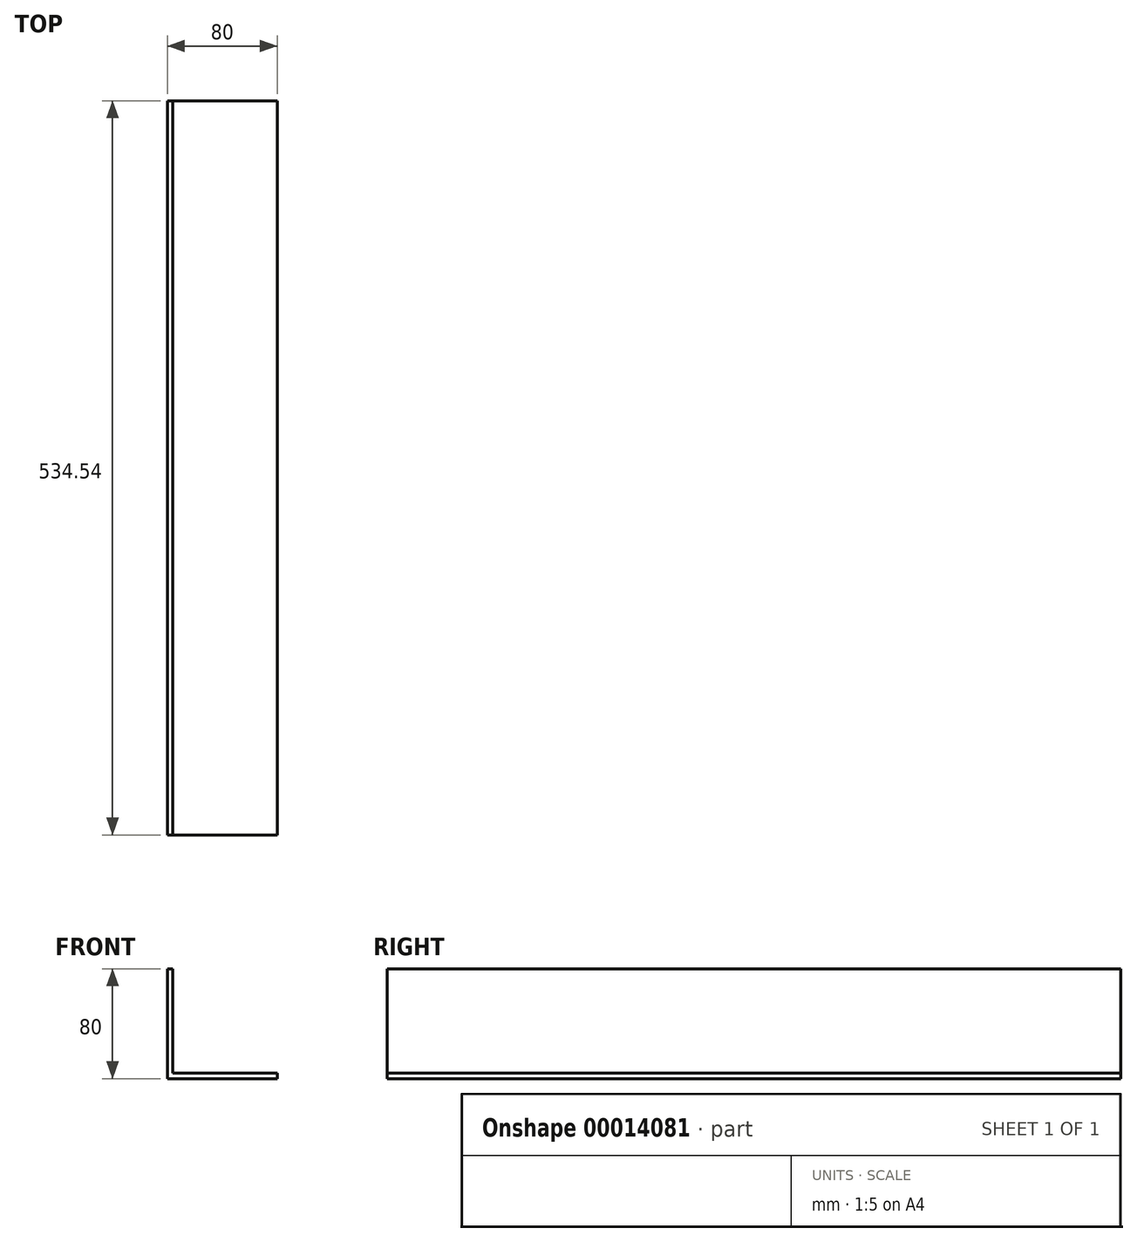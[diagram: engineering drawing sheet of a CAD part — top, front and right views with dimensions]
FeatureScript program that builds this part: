
annotation { "Feature Type Name" : "Feature", "Feature Type Description" : "" }
export const myFeature = defineFeature(function(context is Context, id is Id, definition is map)
    precondition{}
    {
        {
            var Q0;
            Q0=qCreatedBy(makeId("Front.planeOp"),FACE);
            var sketch = newSketch(context, id + "F0", { "sketchPlane" : qUnion([Q0])});
            skLineSegment(sketch, "E0.bottom", {"start": v(0, 0) * mm, "end": v(80, 0) * mm});
            skLineSegment(sketch, "E0.top", {"start": v(0, 80) * mm, "end": v(80, 80) * mm});
            skLineSegment(sketch, "E0.left", {"start": v(0, 0) * mm, "end": v(0, 80) * mm});
            skLineSegment(sketch, "E0.right", {"start": v(80, 0) * mm, "end": v(80, 80) * mm});
            skSolve(sketch);
        }
        {
            var Q0;
            Q0 = qSketchRegion(id + "F0", true);
            extrude(context, id + "F1", {"entities" : qUnion([Q0]), "depth" : 534.53 * mm, "symmetric" : true});
        }
        {
            var Q0;
            Q0=makeQuery(id+"F1.opExtrude","SWEPT_FACE",FACE,{"disambiguationData":[OSD([sQuery(id+"F0.wireOp",EDGE,"E0.top")])]});
            var Q1;
            Q1=makeQuery(id+"F1.opExtrude","SWEPT_FACE",FACE,{"disambiguationData":[OSD([sQuery(id+"F0.wireOp",EDGE,"E0.right")])]});
            var Q2;
            Q2=makeQuery(id+"F1.opExtrude","CAP_FACE",FACE,{"disambiguationData":[OSD([sQuery(id+"F0.wireOp",EDGE,"E0.bottom"),sQuery(id+"F0.wireOp",EDGE,"E0.top"),sQuery(id+"F0.wireOp",EDGE,"E0.left"),sQuery(id+"F0.wireOp",EDGE,"E0.right")])],"isStart":false});
            var Q3;
            Q3=makeQuery(id+"F1.opExtrude","CAP_FACE",FACE,{"disambiguationData":[OSD([sQuery(id+"F0.wireOp",EDGE,"E0.bottom"),sQuery(id+"F0.wireOp",EDGE,"E0.top"),sQuery(id+"F0.wireOp",EDGE,"E0.left"),sQuery(id+"F0.wireOp",EDGE,"E0.right")])],"isStart":true});
            shell(context, id + "F2", {"entities" : qUnion([Q0, Q1, Q2, Q3]), "thickness" : 4 * mm});
        }
    });
